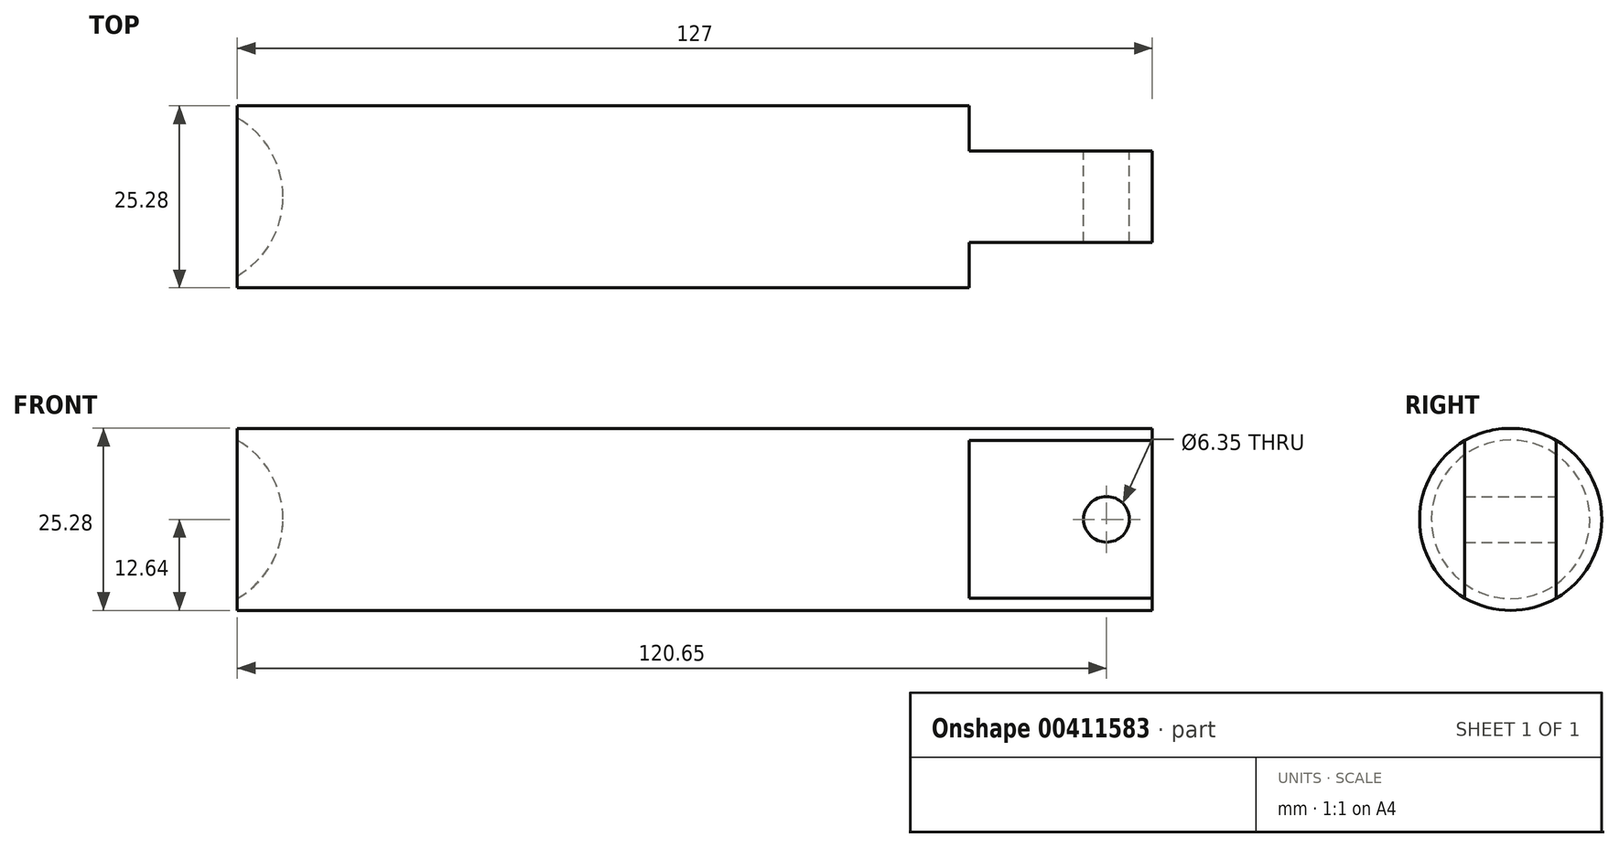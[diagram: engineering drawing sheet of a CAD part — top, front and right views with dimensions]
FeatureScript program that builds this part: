
annotation { "Feature Type Name" : "Feature", "Feature Type Description" : "" }
export const myFeature = defineFeature(function(context is Context, id is Id, definition is map)
    precondition{}
    {
        {
            var Q0;
            Q0=qCreatedBy(makeId("Front.planeOp"),FACE);
            var sketch = newSketch(context, id + "F0", { "sketchPlane" : qUnion([Q0])});
            skLineSegment(sketch, "E0.bottom", {"start": v(-127, 0) * mm, "end": v(0, 0) * mm});
            skLineSegment(sketch, "E0.top", {"start": v(-127, 12.64) * mm, "end": v(0, 12.64) * mm});
            skLineSegment(sketch, "E0.left", {"start": v(-127, 0) * mm, "end": v(-127, 12.64) * mm});
            skLineSegment(sketch, "E0.right", {"start": v(0, 0) * mm, "end": v(0, 12.64) * mm});
            skSolve(sketch);
        }
        {
            var Q0;
            Q0 = qSketchRegion(id + "F0", true);
            var Q1;
            Q1=sQuery(id+"F0.wireOp",EDGE,"E0.bottom");
            revolve(context, id + "F1", {"entities" : qUnion([Q0]), "axis" : qUnion([Q1]), "revolveType" : RevolveType.FULL});
        }
        {
            var Q0;
            Q0=qCreatedBy(makeId("Top.planeOp"),FACE);
            var sketch = newSketch(context, id + "F2", { "sketchPlane" : qUnion([Q0])});
            skLineSegment(sketch, "E1.bottom", {"start": v(0, 6.35) * mm, "end": v(-25.4, 6.35) * mm});
            skLineSegment(sketch, "E1.top", {"start": v(0, 15.42) * mm, "end": v(-25.4, 15.42) * mm});
            skLineSegment(sketch, "E1.left", {"start": v(0, 6.35) * mm, "end": v(0, 15.42) * mm});
            skLineSegment(sketch, "E1.right", {"start": v(-25.4, 6.35) * mm, "end": v(-25.4, 15.42) * mm});
            skLineSegment(sketch, "E2.bottom", {"start": v(0, -6.35) * mm, "end": v(-25.4, -6.35) * mm});
            skLineSegment(sketch, "E2.top", {"start": v(0, -19.53) * mm, "end": v(-25.4, -19.53) * mm});
            skLineSegment(sketch, "E2.left", {"start": v(0, -6.35) * mm, "end": v(0, -19.53) * mm});
            skLineSegment(sketch, "E2.right", {"start": v(-25.4, -6.35) * mm, "end": v(-25.4, -19.53) * mm});
            skSolve(sketch);
        }
        {
            var Q0;
            Q0 = qSketchRegion(id + "F2", true);
            extrude(context, id + "F3", {"entities" : qUnion([Q0]), "operationType" : NewBodyOperationType.REMOVE, "endBound" : BoundingType.SYMMETRIC, "oppositeDirection" : true, "depth" : 12700 * mm});
        }
        {
            var Q0;
            Q0=makeQuery(id+"F3.boolean.opBoolean","COPY",FACE,{"derivedFrom":makeQuery(id+"F3.opExtrude","SWEPT_FACE",FACE,{"disambiguationData":[OSD([sQuery(id+"F2.wireOp",EDGE,"E1.bottom")])]})});
            var sketch = newSketch(context, id + "F4", { "sketchPlane" : qUnion([Q0])});
            skCircle(sketch, "E3", {"center": v(6.35, 0) * mm, "radius": 3.18 * mm});
            skSolve(sketch);
        }
        {
            var Q0;
            Q0 = qSketchRegion(id + "F4", true);
            extrude(context, id + "F5", {"entities" : qUnion([Q0]), "operationType" : NewBodyOperationType.REMOVE, "endBound" : BoundingType.THROUGH_ALL, "oppositeDirection" : true, "depth" : 25.4 * mm});
        }
        {
            var Q0;
            Q0=qCreatedBy(makeId("Front.planeOp"),FACE);
            var sketch = newSketch(context, id + "F6", { "sketchPlane" : qUnion([Q0])});
            skArc(sketch, "E4", {"start": v(-120.65, 0) * mm, "mid": v(-133.35, 12.7) * mm, "end": v(-146.05, 0) * mm});
            skLineSegment(sketch, "E5", {"start": v(-146.05, 0) * mm, "end": v(-120.65, 0) * mm});
            skSolve(sketch);
        }
        {
            var Q0;
            Q0=makeQuery(id+"F6.imprint","IMPRINT",FACE,{"disambiguationData":[TD([[makeQuery(id+"F6.imprint","IMPRINT",EDGE,{"derivedFrom":sQuery(id+"F6.wireOp",EDGE,"E4")}),1.0]])]});
            var Q1;
            Q1=sQuery(id+"F6.wireOp",EDGE,"E5");
            revolve(context, id + "F7", {"operationType" : NewBodyOperationType.REMOVE, "entities" : qUnion([Q0]), "axis" : qUnion([Q1]), "revolveType" : RevolveType.FULL, "oppositeDirection" : true});
        }
    });
